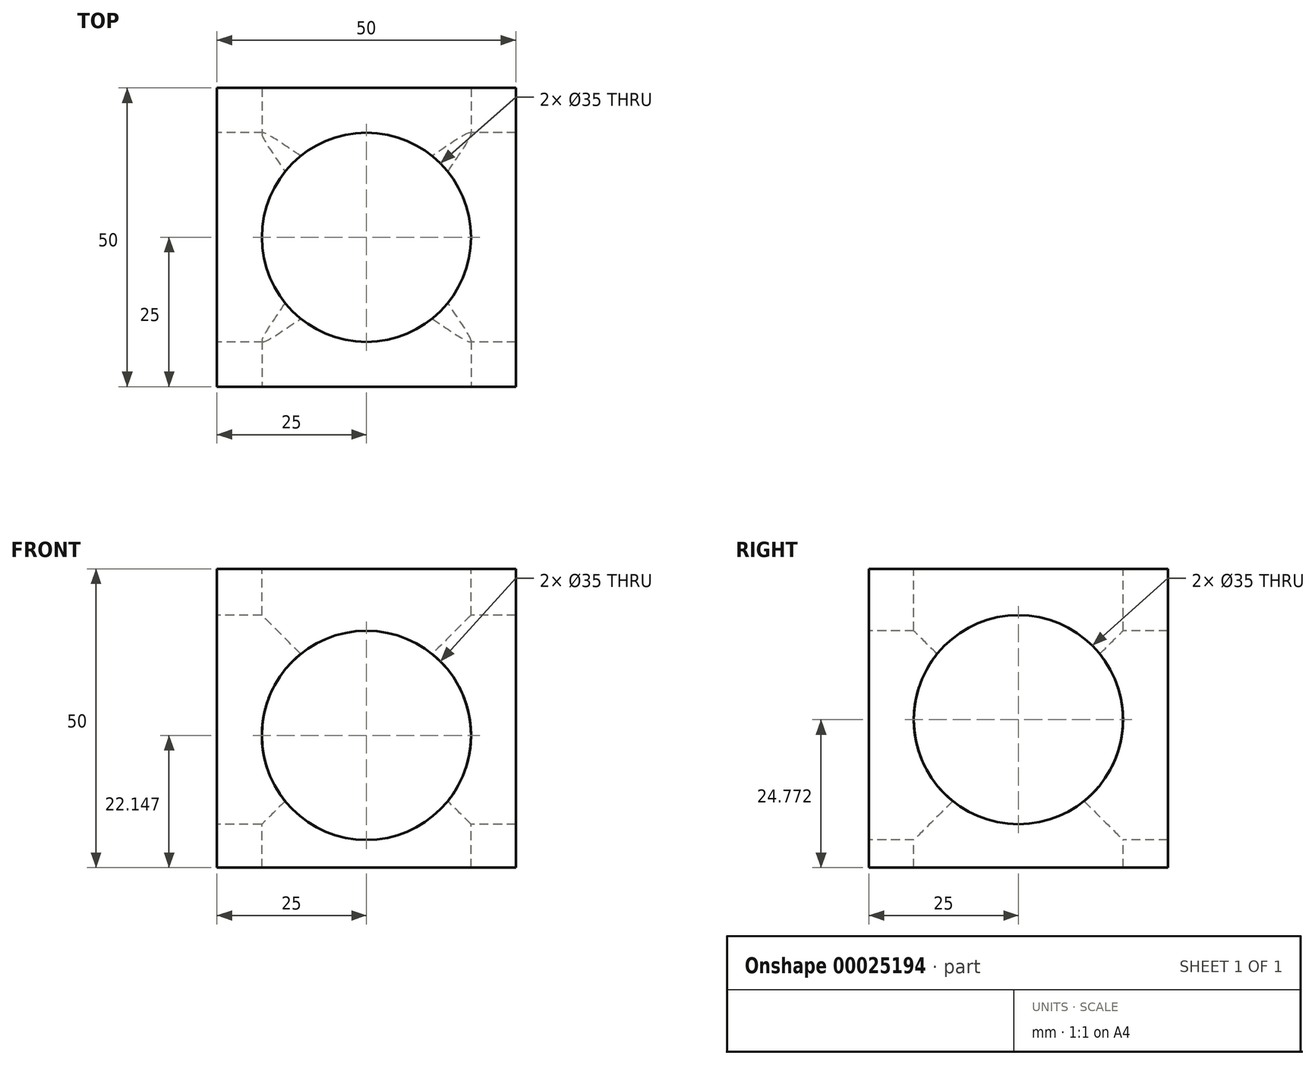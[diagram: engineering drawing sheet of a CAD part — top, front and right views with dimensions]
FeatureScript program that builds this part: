
annotation { "Feature Type Name" : "Feature", "Feature Type Description" : "" }
export const myFeature = defineFeature(function(context is Context, id is Id, definition is map)
    precondition{}
    {
        {
            var Q0;
            Q0=qCreatedBy(makeId("Top.planeOp"),FACE);
            var sketch = newSketch(context, id + "F0", { "sketchPlane" : qUnion([Q0])});
            skLineSegment(sketch, "E0.rect.bottom", {"start": v(-25, 25) * mm, "end": v(25, 25) * mm});
            skLineSegment(sketch, "E0.rect.top", {"start": v(-25, -25) * mm, "end": v(25, -25) * mm});
            skLineSegment(sketch, "E0.rect.left", {"start": v(-25, 25) * mm, "end": v(-25, -25) * mm});
            skLineSegment(sketch, "E0.rect.right", {"start": v(25, 25) * mm, "end": v(25, -25) * mm});
            skPoint(sketch, "E0.rect.middle", {"position": v(0, 0) * mm});
            skSolve(sketch);
        }
        {
            var Q0;
            Q0=makeQuery(id+"F0.imprint","IMPRINT",FACE,{"disambiguationData":[TD([[makeQuery(id+"F0.imprint","IMPRINT",EDGE,{"derivedFrom":sQuery(id+"F0.wireOp",EDGE,"E0.rect.bottom")}),-1.0]])]});
            extrude(context, id + "F1", {"entities" : qUnion([Q0]), "depth" : 50 * mm});
        }
        {
            var Q0;
            Q0=makeQuery(id+"F1.opExtrude","CAP_FACE",FACE,{"disambiguationData":[OSD([sQuery(id+"F0.wireOp",EDGE,"E0.rect.bottom"),sQuery(id+"F0.wireOp",EDGE,"E0.rect.top"),sQuery(id+"F0.wireOp",EDGE,"E0.rect.left"),sQuery(id+"F0.wireOp",EDGE,"E0.rect.right")])],"isStart":false});
            var sketch = newSketch(context, id + "F2", { "sketchPlane" : qUnion([Q0])});
            skCircle(sketch, "E1", {"center": v(0, 0) * mm, "radius": 17.5 * mm});
            skSolve(sketch);
        }
        {
            var Q0;
            Q0=makeQuery(id+"F2.imprint","IMPRINT",FACE,{"disambiguationData":[TD([[makeQuery(id+"F2.imprint","IMPRINT",EDGE,{"derivedFrom":sQuery(id+"F2.wireOp",EDGE,"E1")}),1.0]])]});
            extrude(context, id + "F3", {"entities" : qUnion([Q0]), "operationType" : NewBodyOperationType.REMOVE, "oppositeDirection" : true, "depth" : 50 * mm});
        }
        {
            var Q0;
            Q0=makeQuery(id+"F1.opExtrude","SWEPT_FACE",FACE,{"disambiguationData":[OSD([sQuery(id+"F0.wireOp",EDGE,"E0.rect.top")])]});
            var sketch = newSketch(context, id + "F4", { "sketchPlane" : qUnion([Q0])});
            skCircle(sketch, "E2", {"center": v(0, 22.15) * mm, "radius": 17.5 * mm});
            skSolve(sketch);
        }
        {
            var Q0;
            Q0=makeQuery(id+"F4.imprint","IMPRINT",FACE,{"disambiguationData":[TD([[makeQuery(id+"F4.imprint","IMPRINT",EDGE,{"derivedFrom":sQuery(id+"F4.wireOp",EDGE,"E2")}),1.0]])]});
            extrude(context, id + "F5", {"entities" : qUnion([Q0]), "operationType" : NewBodyOperationType.REMOVE, "oppositeDirection" : true, "depth" : 50 * mm});
        }
        {
            var Q0;
            Q0=makeQuery(id+"F1.opExtrude","SWEPT_FACE",FACE,{"disambiguationData":[OSD([sQuery(id+"F0.wireOp",EDGE,"E0.rect.left")])]});
            var sketch = newSketch(context, id + "F6", { "sketchPlane" : qUnion([Q0])});
            skCircle(sketch, "E3", {"center": v(0, 24.77) * mm, "radius": 17.5 * mm});
            skSolve(sketch);
        }
        {
            var Q0;
            Q0=makeQuery(id+"F6.imprint","IMPRINT",FACE,{"disambiguationData":[TD([[makeQuery(id+"F6.imprint","IMPRINT",EDGE,{"derivedFrom":sQuery(id+"F6.wireOp",EDGE,"E3")}),1.0]])]});
            extrude(context, id + "F7", {"entities" : qUnion([Q0]), "operationType" : NewBodyOperationType.REMOVE, "oppositeDirection" : true, "depth" : 50 * mm});
        }
    });
